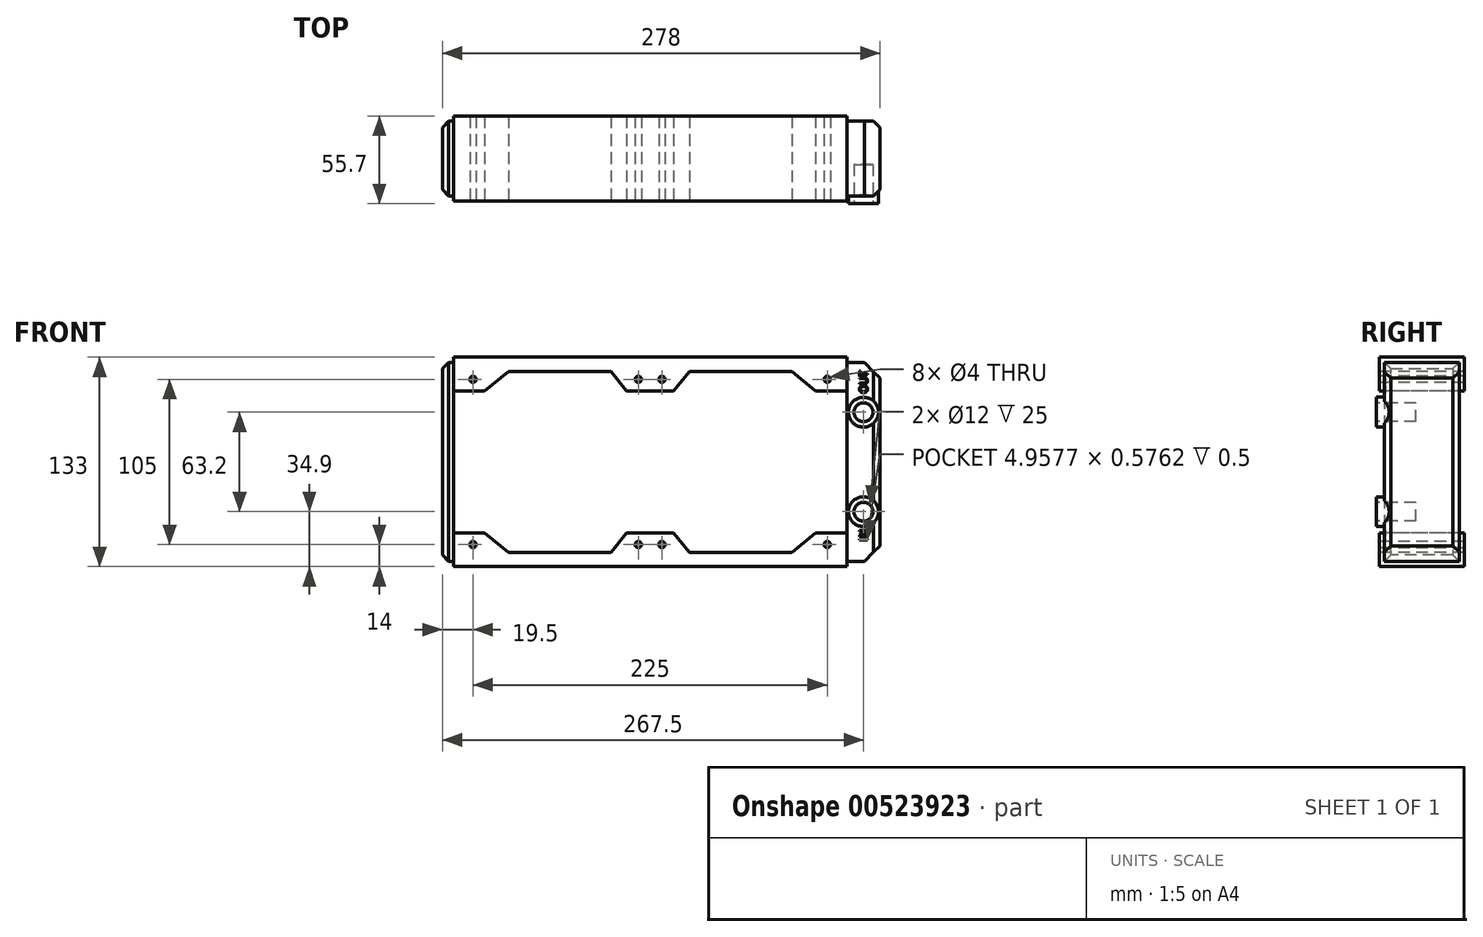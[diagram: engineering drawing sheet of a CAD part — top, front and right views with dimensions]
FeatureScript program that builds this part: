
annotation { "Feature Type Name" : "Feature", "Feature Type Description" : "" }
export const myFeature = defineFeature(function(context is Context, id is Id, definition is map)
    precondition{}
    {
        {
            var Q0;
            Q0=qCreatedBy(makeId("Front.planeOp"),FACE);
            var sketch = newSketch(context, id + "F0", { "sketchPlane" : qUnion([Q0])});
            skLineSegment(sketch, "E0.bottom", {"start": v(0, 63.2) * mm, "end": v(278, 63.2) * mm});
            skLineSegment(sketch, "E0.top", {"start": v(0, -63.2) * mm, "end": v(278, -63.2) * mm});
            skLineSegment(sketch, "E0.left", {"start": v(0, 63.2) * mm, "end": v(0, -63.2) * mm});
            skLineSegment(sketch, "E0.right", {"start": v(278, 63.2) * mm, "end": v(278, -63.2) * mm});
            skPoint(sketch, "E1", {"position": v(0, 0) * mm});
            skSolve(sketch);
        }
        {
            var Q0;
            Q0=qSketchRegion(id+"F0",true);
            extrude(context, id + "F1", {"entities" : qUnion([Q0]), "depth" : 47.4 * mm});
        }
        {
            var Q0;
            Q0=makeQuery(id+"F1.opExtrude","CAP_FACE",FACE,{"disambiguationData":[OSD([sQuery(id+"F0.wireOp",EDGE,"E0.bottom"),sQuery(id+"F0.wireOp",EDGE,"E0.top"),sQuery(id+"F0.wireOp",EDGE,"E0.left"),sQuery(id+"F0.wireOp",EDGE,"E0.right")])],"isStart":false});
            var sketch = newSketch(context, id + "F2", { "sketchPlane" : qUnion([Q0])});
            skCircle(sketch, "E2", {"center": v(267.5, 31.6) * mm, "radius": 9.5 * mm});
            skCircle(sketch, "E3", {"center": v(267.5, -31.6) * mm, "radius": 9.5 * mm});
            skLineSegment(sketch, "E4", {"start": v(278, 0) * mm, "end": v(0, 0) * mm, "construction": true});
            skSolve(sketch);
        }
        {
            var Q0;
            Q0=qSketchRegion(id+"F2",true);
            extrude(context, id + "F3", {"entities" : qUnion([Q0]), "operationType" : NewBodyOperationType.ADD, "depth" : 5 * mm});
        }
        {
            var Q0;
            Q0=makeQuery(id+"F3.opExtrude","CAP_FACE",FACE,{"disambiguationData":[OSD([sQuery(id+"F2.wireOp",EDGE,"E2")])],"isStart":false});
            var sketch = newSketch(context, id + "F4", { "sketchPlane" : qUnion([Q0])});
            skCircle(sketch, "E5", {"center": v(267.5, 31.6) * mm, "radius": 6 * mm});
            skCircle(sketch, "E6", {"center": v(267.5, -31.6) * mm, "radius": 6 * mm});
            skSolve(sketch);
        }
        {
            var Q0;
            Q0=qSketchRegion(id+"F4",true);
            extrude(context, id + "F5", {"entities" : qUnion([Q0]), "operationType" : NewBodyOperationType.REMOVE, "oppositeDirection" : true, "depth" : 25 * mm});
        }
        {
            var Q0;
            Q0=makeQuery(id+"F1.opExtrude","SWEPT_EDGE",EDGE,{"disambiguationData":[OSD([sQuery(id+"F0.wireOp",EDGE,"E0.top"),sQuery(id+"F0.wireOp",EDGE,"E0.right")])]});
            var Q1;
            Q1=makeQuery(id+"F1.opExtrude","SWEPT_EDGE",EDGE,{"disambiguationData":[OSD([sQuery(id+"F0.wireOp",EDGE,"E0.bottom"),sQuery(id+"F0.wireOp",EDGE,"E0.right")])]});
            chamfer(context, id + "F6", {"entities" : qUnion([Q0, Q1]), "width" : 10 * mm, "tangentPropagation" : true});
        }
        {
            var Q0;
            Q0=makeQuery(id+"F1.opExtrude","CAP_EDGE",EDGE,{"disambiguationData":[OSD([sQuery(id+"F0.wireOp",EDGE,"E0.right")])],"isStart":false});
            var Q1;
            Q1=makeQuery(id+"F1.opExtrude","CAP_EDGE",EDGE,{"disambiguationData":[OSD([sQuery(id+"F0.wireOp",EDGE,"E0.right")])],"isStart":true});
            var Q2;
            Q2=makeQuery(id+"F1.opExtrude","CAP_EDGE",EDGE,{"disambiguationData":[OSD([sQuery(id+"F0.wireOp",EDGE,"E0.left")])],"isStart":false});
            var Q3;
            Q3=makeQuery(id+"F1.opExtrude","CAP_EDGE",EDGE,{"disambiguationData":[OSD([sQuery(id+"F0.wireOp",EDGE,"E0.left")])],"isStart":true});
            var Q4;
            Q4=makeQuery(id+"F1.opExtrude","SWEPT_EDGE",EDGE,{"disambiguationData":[OSD([sQuery(id+"F0.wireOp",EDGE,"E0.top"),sQuery(id+"F0.wireOp",EDGE,"E0.left")])]});
            var Q5;
            Q5=makeQuery(id+"F1.opExtrude","SWEPT_EDGE",EDGE,{"disambiguationData":[OSD([sQuery(id+"F0.wireOp",EDGE,"E0.bottom"),sQuery(id+"F0.wireOp",EDGE,"E0.left")])]});
            chamfer(context, id + "F7", {"entities" : qUnion([Q0, Q1, Q2, Q3, Q4, Q5]), "width" : 4 * mm, "tangentPropagation" : true});
        }
        {
            var Q0;
            Q0=makeQuery(id+"F1.opExtrude","SWEPT_FACE",FACE,{"disambiguationData":[OSD([sQuery(id+"F0.wireOp",EDGE,"E0.left")])]});
            cPlane(context, id + "F8", {"entities" : qUnion([Q0]), "cplaneType" : CPlaneType.OFFSET, "offset" : 7 * mm, "oppositeDirection" : true, "width" : 150 * mm, "height" : 150 * mm});
        }
        {
            var Q0;
            Q0=qCreatedBy(id+"F8.planeOp",FACE);
            var sketch = newSketch(context, id + "F9", { "sketchPlane" : qUnion([Q0])});
            skLineSegment(sketch, "E7.bottom", {"start": v(-3.3, 66.5) * mm, "end": v(50.7, 66.5) * mm});
            skLineSegment(sketch, "E7.top", {"start": v(-3.3, -66.5) * mm, "end": v(50.7, -66.5) * mm});
            skLineSegment(sketch, "E7.left", {"start": v(-3.3, 66.5) * mm, "end": v(-3.3, -66.5) * mm});
            skLineSegment(sketch, "E7.right", {"start": v(50.7, 66.5) * mm, "end": v(50.7, -66.5) * mm});
            skLineSegment(sketch, "E8", {"start": v(0, 0) * mm, "end": v(-3.3, 0) * mm, "construction": true});
            skLineSegment(sketch, "E9.bottom", {"start": v(0, 63.2) * mm, "end": v(47.4, 63.2) * mm});
            skLineSegment(sketch, "E9.top", {"start": v(0, -63.2) * mm, "end": v(47.4, -63.2) * mm});
            skLineSegment(sketch, "E9.left", {"start": v(0, 63.2) * mm, "end": v(0, -63.2) * mm});
            skLineSegment(sketch, "E9.right", {"start": v(47.4, 63.2) * mm, "end": v(47.4, -63.2) * mm});
            skSolve(sketch);
        }
        {
            var Q0;
            Q0=qSketchRegion(id+"F9",true);
            extrude(context, id + "F10", {"entities" : qUnion([Q0]), "oppositeDirection" : true, "depth" : 250 * mm});
        }
        {
            var Q0;
            Q0=makeQuery(id+"F10.opExtrude","SWEPT_FACE",FACE,{"disambiguationData":[OSD([sQuery(id+"F9.wireOp",EDGE,"E7.right")])]});
            var sketch = newSketch(context, id + "F11", { "sketchPlane" : qUnion([Q0])});
            skCircle(sketch, "E10", {"center": v(19.5, 52.5) * mm, "radius": 2 * mm});
            skCircle(sketch, "E11", {"center": v(124.5, 52.5) * mm, "radius": 2 * mm});
            skCircle(sketch, "E12", {"center": v(139.5, 52.5) * mm, "radius": 2 * mm});
            skCircle(sketch, "E13", {"center": v(244.5, 52.5) * mm, "radius": 2 * mm});
            skLineSegment(sketch, "E14", {"start": v(7, 0) * mm, "end": v(257, 0) * mm, "construction": true});
            skLineSegment(sketch, "E15", {"start": v(132, 66.5) * mm, "end": v(132, -66.5) * mm, "construction": true});
            skCircle(sketch, "E16.MirrorC", {"center": v(19.5, -52.5) * mm, "radius": 2 * mm});
            skCircle(sketch, "E17.MirrorC", {"center": v(124.5, -52.5) * mm, "radius": 2 * mm});
            skCircle(sketch, "E18.MirrorC", {"center": v(139.5, -52.5) * mm, "radius": 2 * mm});
            skCircle(sketch, "E19.MirrorC", {"center": v(244.5, -52.5) * mm, "radius": 2 * mm});
            skSolve(sketch);
        }
        {
            var Q0;
            Q0=qSketchRegion(id+"F11",true);
            extrude(context, id + "F12", {"entities" : qUnion([Q0]), "operationType" : NewBodyOperationType.REMOVE, "endBound" : BoundingType.THROUGH_ALL, "oppositeDirection" : true, "depth" : 25 * mm});
        }
        {
            var Q0;
            Q0=makeQuery(id+"F10.opExtrude","SWEPT_FACE",FACE,{"disambiguationData":[OSD([sQuery(id+"F9.wireOp",EDGE,"E7.right")])]});
            var sketch = newSketch(context, id + "F13", { "sketchPlane" : qUnion([Q0])});
            skLineSegment(sketch, "E20", {"start": v(7, 45) * mm, "end": v(27, 45) * mm});
            skLineSegment(sketch, "E21", {"start": v(27, 45) * mm, "end": v(42, 57.5) * mm});
            skLineSegment(sketch, "E22", {"start": v(42, 57.5) * mm, "end": v(107, 57.5) * mm});
            skLineSegment(sketch, "E23", {"start": v(107, 57.5) * mm, "end": v(117, 45) * mm});
            skLineSegment(sketch, "E24", {"start": v(117, 45) * mm, "end": v(147, 45) * mm});
            skLineSegment(sketch, "E25", {"start": v(147, 45) * mm, "end": v(157, 57.5) * mm});
            skLineSegment(sketch, "E26", {"start": v(157, 57.5) * mm, "end": v(222, 57.5) * mm});
            skLineSegment(sketch, "E27", {"start": v(222, 57.5) * mm, "end": v(237, 45) * mm});
            skLineSegment(sketch, "E28", {"start": v(237, 45) * mm, "end": v(257, 45) * mm});
            skLineSegment(sketch, "E29", {"start": v(257, 45) * mm, "end": v(257, 0) * mm});
            skLineSegment(sketch, "E30", {"start": v(7, 45) * mm, "end": v(7, 0) * mm});
            skLineSegment(sketch, "E31", {"start": v(7, 0) * mm, "end": v(257, 0) * mm, "construction": true});
            skLineSegment(sketch, "E32", {"start": v(132, 66.5) * mm, "end": v(132, 45) * mm, "construction": true});
            skLineSegment(sketch, "E33.MirrorCS", {"start": v(257, -45) * mm, "end": v(257, 0) * mm});
            skLineSegment(sketch, "E34.MirrorCS", {"start": v(237, -45) * mm, "end": v(257, -45) * mm});
            skLineSegment(sketch, "E35.MirrorCS", {"start": v(222, -57.5) * mm, "end": v(237, -45) * mm});
            skLineSegment(sketch, "E36.MirrorCS", {"start": v(157, -57.5) * mm, "end": v(222, -57.5) * mm});
            skLineSegment(sketch, "E37.MirrorCS", {"start": v(147, -45) * mm, "end": v(157, -57.5) * mm});
            skLineSegment(sketch, "E38.MirrorCS", {"start": v(117, -45) * mm, "end": v(147, -45) * mm});
            skLineSegment(sketch, "E39.MirrorCS", {"start": v(107, -57.5) * mm, "end": v(117, -45) * mm});
            skLineSegment(sketch, "E40.MirrorCS", {"start": v(42, -57.5) * mm, "end": v(107, -57.5) * mm});
            skLineSegment(sketch, "E41.MirrorCS", {"start": v(27, -45) * mm, "end": v(42, -57.5) * mm});
            skLineSegment(sketch, "E42.MirrorCS", {"start": v(7, -45) * mm, "end": v(7, 0) * mm});
            skLineSegment(sketch, "E43.MirrorCS", {"start": v(7, -45) * mm, "end": v(27, -45) * mm});
            skSolve(sketch);
        }
        {
            var Q0;
            Q0=qSketchRegion(id+"F13",true);
            extrude(context, id + "F14", {"entities" : qUnion([Q0]), "operationType" : NewBodyOperationType.REMOVE, "endBound" : BoundingType.THROUGH_ALL, "oppositeDirection" : true, "depth" : 25 * mm});
        }
        {
            var Q0;
            Q0=makeQuery(id+"F1.opExtrude","SWEPT_BODY",BODY,{"disambiguationData":[OSD([sQuery(id+"F0.wireOp",EDGE,"E0.bottom"),sQuery(id+"F0.wireOp",EDGE,"E0.top"),sQuery(id+"F0.wireOp",EDGE,"E0.left"),sQuery(id+"F0.wireOp",EDGE,"E0.right")])]});
            var Q1;
            Q1=makeQuery(id+"F14.boolean.opBoolean","SPLIT",BODY,{"disambiguationData":[OD(0.0)],"derivedFrom":makeQuery(id+"F10.opExtrude","SWEPT_BODY",BODY,{"disambiguationData":[OSD([sQuery(id+"F9.wireOp",EDGE,"E7.bottom"),sQuery(id+"F9.wireOp",EDGE,"E7.top"),sQuery(id+"F9.wireOp",EDGE,"E7.left"),sQuery(id+"F9.wireOp",EDGE,"E7.right"),sQuery(id+"F9.wireOp",EDGE,"E9.bottom"),sQuery(id+"F9.wireOp",EDGE,"E9.top"),sQuery(id+"F9.wireOp",EDGE,"E9.left"),sQuery(id+"F9.wireOp",EDGE,"E9.right")])]})});
            var Q2;
            Q2=makeQuery(id+"F14.boolean.opBoolean","SPLIT",BODY,{"disambiguationData":[OD(1.0)],"derivedFrom":makeQuery(id+"F10.opExtrude","SWEPT_BODY",BODY,{"disambiguationData":[OSD([sQuery(id+"F9.wireOp",EDGE,"E7.bottom"),sQuery(id+"F9.wireOp",EDGE,"E7.top"),sQuery(id+"F9.wireOp",EDGE,"E7.left"),sQuery(id+"F9.wireOp",EDGE,"E7.right"),sQuery(id+"F9.wireOp",EDGE,"E9.bottom"),sQuery(id+"F9.wireOp",EDGE,"E9.top"),sQuery(id+"F9.wireOp",EDGE,"E9.left"),sQuery(id+"F9.wireOp",EDGE,"E9.right")])]})});
            booleanBodies(context, id + "F15", {"operationType" : BooleanOperationType.UNION, "tools" : qUnion([Q0, Q1, Q2])});
        }
        {
            var Q0;
            {var subQ8=sQuery(id+"F0.wireOp",EDGE,"E0.top");var subQ9=sQuery(id+"F0.wireOp",EDGE,"E0.right");var subQ10=sQuery(id+"F0.wireOp",EDGE,"E0.left");var subQ11=sQuery(id+"F0.wireOp",EDGE,"E0.bottom");Q0=makeQuery(id+"F15.opBoolean","SPLIT",FACE,{"disambiguationData":[TD([makeQuery(id+"F1.opExtrude","SWEPT_FACE",FACE,{"disambiguationData":[OSD([subQ11])]})])],"derivedFrom":makeQuery(id+"F1.opExtrude","CAP_FACE",FACE,{"disambiguationData":[OSD([subQ11,subQ8,subQ10,subQ9])],"isStart":false})});}
            var sketch = newSketch(context, id + "F16", { "sketchPlane" : qUnion([Q0])});
            skText(sketch, "E44", { "text": "IN", "fontName": "OpenSans-Regular.ttf"});
            skPoint(sketch, "E45", {"position": v(267.5, -31.6) * mm});
            skPoint(sketch, "E46", {"position": v(267.5, 31.6) * mm});
            skPoint(sketch, "E47", {"position": v(267.5, -43.6) * mm});
            skText(sketch, "E48", { "text": "OUT", "fontName": "OpenSans-Regular.ttf"});
            skPoint(sketch, "E49", {"position": v(267.52, 127.37) * mm});
            skPoint(sketch, "E50", {"position": v(267.5, 43.6) * mm});
            const initialGuessF16  = {"E44": [0.27, -0.05009, 0, 1, 0.005], "E48": [0.27, 0.0436, 0, 1, 0.005]};
            skSetInitialGuess(sketch, initialGuessF16);
            skSolve(sketch);
        }
        {
            var Q0;
            Q0=qSketchRegion(id+"F16",true);
            extrude(context, id + "F17", {"entities" : qUnion([Q0]), "operationType" : NewBodyOperationType.REMOVE, "oppositeDirection" : true, "depth" : .5 * mm});
        }
    });
